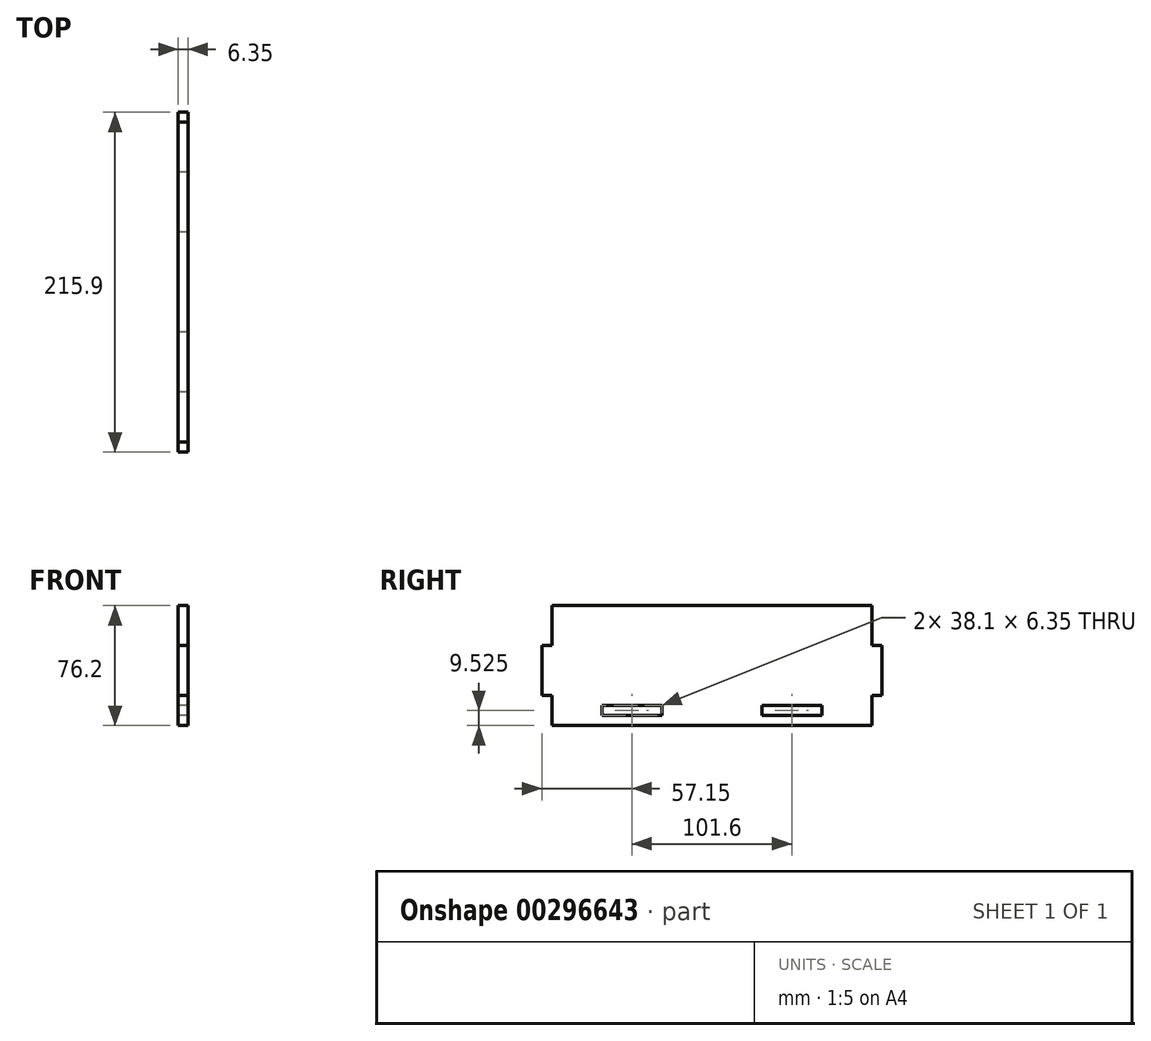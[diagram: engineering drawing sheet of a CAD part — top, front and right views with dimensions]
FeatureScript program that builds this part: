
annotation { "Feature Type Name" : "Feature", "Feature Type Description" : "" }
export const myFeature = defineFeature(function(context is Context, id is Id, definition is map)
    precondition{}
    {
        {
            var Q0;
            Q0=qCreatedBy(makeId("Right.planeOp"),FACE);
            var sketch = newSketch(context, id + "F0", { "sketchPlane" : qUnion([Q0])});
            skLineSegment(sketch, "E0.bottom", {"start": v(-101.6, 38.1) * mm, "end": v(101.6, 38.1) * mm});
            skLineSegment(sketch, "E0.top", {"start": v(-101.6, -38.1) * mm, "end": v(101.6, -38.1) * mm});
            skLineSegment(sketch, "E0.left", {"start": v(-101.6, 38.1) * mm, "end": v(-101.6, 12.7) * mm});
            skLineSegment(sketch, "E0.right", {"start": v(101.6, 38.1) * mm, "end": v(101.6, 12.7) * mm});
            skPoint(sketch, "E0.middle", {"position": v(0, 0) * mm});
            skLineSegment(sketch, "E1", {"start": v(-101.6, -28.57) * mm, "end": v(101.6, -28.58) * mm, "construction": true});
            skLineSegment(sketch, "E2.bottom", {"start": v(-101.6, 12.7) * mm, "end": v(-107.95, 12.7) * mm});
            skLineSegment(sketch, "E2.top", {"start": v(-101.6, -19.05) * mm, "end": v(-107.95, -19.05) * mm});
            skLineSegment(sketch, "E2.right", {"start": v(-107.95, 12.7) * mm, "end": v(-107.95, -19.05) * mm});
            skPoint(sketch, "E3", {"position": v(-107.95, -3.17) * mm});
            skLineSegment(sketch, "E4.trimOffspring", {"start": v(-101.6, -19.05) * mm, "end": v(-101.6, -38.1) * mm});
            skPoint(sketch, "E5.MirrorP", {"position": v(107.95, -3.17) * mm});
            skLineSegment(sketch, "E6.MirrorCS", {"start": v(101.6, 12.7) * mm, "end": v(107.95, 12.7) * mm});
            skLineSegment(sketch, "E7.MirrorCS", {"start": v(101.6, -19.05) * mm, "end": v(107.95, -19.05) * mm});
            skLineSegment(sketch, "E8.MirrorCS", {"start": v(107.95, 12.7) * mm, "end": v(107.95, -19.05) * mm});
            skLineSegment(sketch, "E9.trimOffspring", {"start": v(101.6, -19.05) * mm, "end": v(101.6, -38.1) * mm});
            skLineSegment(sketch, "E10.bottom", {"start": v(-31.75, -25.4) * mm, "end": v(-69.85, -25.4) * mm});
            skLineSegment(sketch, "E10.top", {"start": v(-31.75, -31.75) * mm, "end": v(-69.85, -31.75) * mm});
            skLineSegment(sketch, "E10.left", {"start": v(-31.75, -25.4) * mm, "end": v(-31.75, -31.75) * mm});
            skLineSegment(sketch, "E10.right", {"start": v(-69.85, -25.4) * mm, "end": v(-69.85, -31.75) * mm});
            skPoint(sketch, "E10.middle", {"position": v(-50.8, -28.57) * mm});
            skLineSegment(sketch, "E11.MirrorCS", {"start": v(69.85, -25.4) * mm, "end": v(69.85, -31.75) * mm});
            skLineSegment(sketch, "E12.MirrorCS", {"start": v(31.75, -25.4) * mm, "end": v(31.75, -31.75) * mm});
            skLineSegment(sketch, "E13.MirrorCS", {"start": v(31.75, -31.75) * mm, "end": v(69.85, -31.75) * mm});
            skLineSegment(sketch, "E14.MirrorCS", {"start": v(31.75, -25.4) * mm, "end": v(69.85, -25.4) * mm});
            skPoint(sketch, "E15.MirrorP", {"position": v(50.8, -28.57) * mm});
            skSolve(sketch);
        }
        {
            var Q0;
            Q0 = qSketchRegion(id + "F0", true);
            extrude(context, id + "F1", {"entities" : qUnion([Q0]), "depth" : 6.35 * mm});
        }
    });
